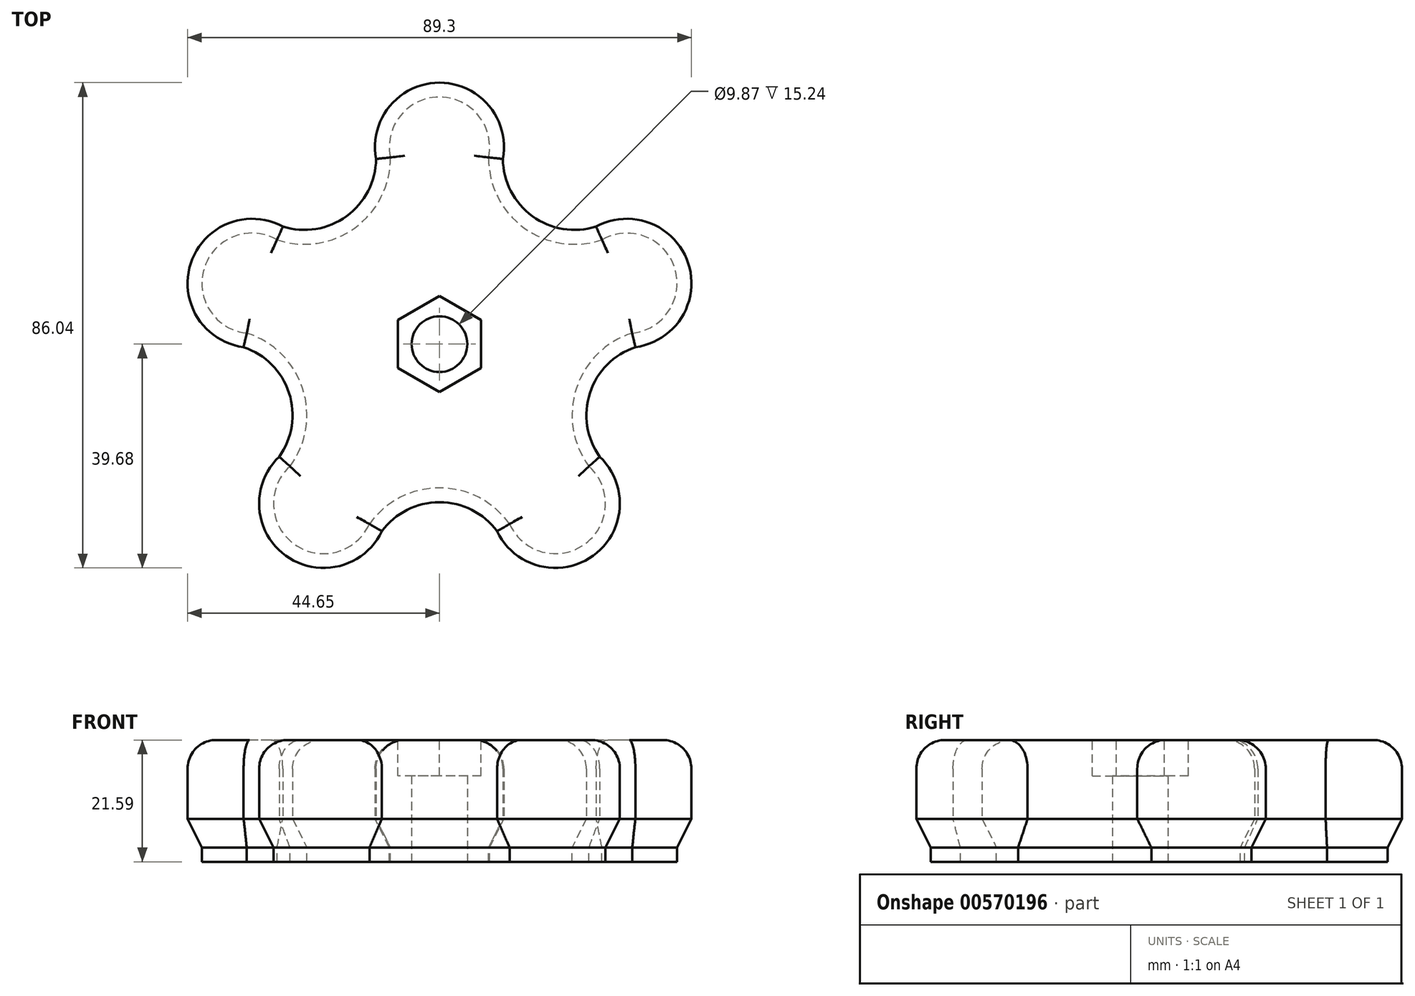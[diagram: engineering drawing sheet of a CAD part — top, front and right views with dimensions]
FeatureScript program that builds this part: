
annotation { "Feature Type Name" : "Feature", "Feature Type Description" : "" }
export const myFeature = defineFeature(function(context is Context, id is Id, definition is map)
    precondition{}
    {
        {
            var Q0;
            Q0=qCreatedBy(makeId("Top.planeOp"),FACE);
            var sketch = newSketch(context, id + "F0", { "sketchPlane" : qUnion([Q0])});
            skArc(sketch, "E0", {"start": v(11.24, 32.85) * mm, "mid": v(0, 46.36) * mm, "end": v(-11.24, 32.85) * mm});
            skArc(sketch, "E1.1.0", {"start": v(34.71, -0.54) * mm, "mid": v(44.09, 14.32) * mm, "end": v(27.77, 20.84) * mm});
            skArc(sketch, "E1.2.0", {"start": v(10.21, -33.18) * mm, "mid": v(27.25, -37.5) * mm, "end": v(28.4, -19.97) * mm});
            skArc(sketch, "E1.3.0", {"start": v(-28.4, -19.97) * mm, "mid": v(-27.25, -37.5) * mm, "end": v(-10.21, -33.18) * mm});
            skArc(sketch, "E1.4.0", {"start": v(-27.77, 20.84) * mm, "mid": v(-44.09, 14.32) * mm, "end": v(-34.71, -0.54) * mm});
            skPoint(sketch, "E1.center", {"position": v(0, 0) * mm});
            skLineSegment(sketch, "E1.anchor1", {"start": v(0, 0) * mm, "end": v(0, 34.93) * mm, "construction": true});
            skLineSegment(sketch, "E1.anchor2", {"start": v(0, 0) * mm, "end": v(-33.22, 10.8) * mm, "construction": true});
            skArc(sketch, "E2", {"start": v(-27.77, 20.84) * mm, "mid": v(-16.47, 22.67) * mm, "end": v(-11.24, 32.85) * mm});
            skArc(sketch, "E3.1.0", {"start": v(-28.4, -19.97) * mm, "mid": v(-26.66, -8.66) * mm, "end": v(-34.71, -0.54) * mm});
            skArc(sketch, "E3.2.0", {"start": v(10.21, -33.18) * mm, "mid": v(0, -28.03) * mm, "end": v(-10.21, -33.18) * mm});
            skArc(sketch, "E3.3.0", {"start": v(34.71, -0.54) * mm, "mid": v(26.66, -8.66) * mm, "end": v(28.4, -19.97) * mm});
            skArc(sketch, "E3.4.0", {"start": v(11.24, 32.85) * mm, "mid": v(16.47, 22.67) * mm, "end": v(27.77, 20.84) * mm});
            skCircle(sketch, "E4", {"center": v(0, 0) * mm, "radius": 4.93 * mm});
            skSolve(sketch);
        }
        {
            var Q0;
            Q0=makeQuery(id+"F0.imprint","IMPRINT",FACE,{"disambiguationData":[TD([[makeQuery(id+"F0.imprint","IMPRINT",EDGE,{"derivedFrom":sQuery(id+"F0.wireOp",EDGE,"E0")}),1.0]])]});
            extrude(context, id + "F1", {"entities" : qUnion([Q0]), "depth" : 19.05 * mm, "offsetDistance" : 25.4 * mm});
        }
        {
            var Q0;
            Q0=makeQuery(id+"F1.opExtrude","CAP_FACE",FACE,{"disambiguationData":[OSD([sQuery(id+"F0.wireOp",EDGE,"E0"),sQuery(id+"F0.wireOp",EDGE,"E1.1.0"),sQuery(id+"F0.wireOp",EDGE,"E1.2.0"),sQuery(id+"F0.wireOp",EDGE,"E1.3.0"),sQuery(id+"F0.wireOp",EDGE,"E1.4.0"),sQuery(id+"F0.wireOp",EDGE,"E2"),sQuery(id+"F0.wireOp",EDGE,"E3.1.0"),sQuery(id+"F0.wireOp",EDGE,"E3.2.0"),sQuery(id+"F0.wireOp",EDGE,"E3.3.0"),sQuery(id+"F0.wireOp",EDGE,"E3.4.0"),sQuery(id+"F0.wireOp",EDGE,"E4")])],"isStart":false});
            var sketch = newSketch(context, id + "F2", { "sketchPlane" : qUnion([Q0])});
            skCircle(sketch, "E5.cCircle", {"center": v(0, 0) * mm, "radius": 7.37 * mm, "construction": true});
            skLineSegment(sketch, "E5.0", {"start": v(-7.37, -4.25) * mm, "end": v(-7.37, 4.25) * mm});
            skLineSegment(sketch, "E5.1", {"start": v(-7.37, 4.25) * mm, "end": v(0, 8.5) * mm});
            skLineSegment(sketch, "E5.2", {"start": v(0, 8.5) * mm, "end": v(7.37, 4.25) * mm});
            skLineSegment(sketch, "E5.3", {"start": v(7.37, 4.25) * mm, "end": v(7.37, -4.25) * mm});
            skLineSegment(sketch, "E5.4", {"start": v(7.37, -4.25) * mm, "end": v(0, -8.5) * mm});
            skLineSegment(sketch, "E5.5", {"start": v(0, -8.5) * mm, "end": v(-7.37, -4.25) * mm});
            skPoint(sketch, "E5.0.midPoint", {"position": v(-7.37, 0) * mm});
            skSolve(sketch);
        }
        {
            var Q0;
            Q0=makeQuery(id+"F2.imprint","IMPRINT",FACE,{"disambiguationData":[TD([[makeQuery(id+"F2.imprint","IMPRINT",EDGE,{"derivedFrom":sQuery(id+"F2.wireOp",EDGE,"E5.0")}),-1.0]])]});
            extrude(context, id + "F3", {"entities" : qUnion([Q0]), "operationType" : NewBodyOperationType.REMOVE, "oppositeDirection" : true, "depth" : 6.35 * mm, "offsetDistance" : 25.4 * mm});
        }
        {
            var Q0;
            Q0=makeQuery(id+"F1.opExtrude","CAP_EDGE",EDGE,{"disambiguationData":[OSD([sQuery(id+"F0.wireOp",EDGE,"E3.1.0")])],"isStart":false});
            var Q1;
            Q1=makeQuery(id+"F1.opExtrude","CAP_EDGE",EDGE,{"disambiguationData":[OSD([sQuery(id+"F0.wireOp",EDGE,"E1.4.0")])],"isStart":false});
            var Q2;
            Q2=makeQuery(id+"F1.opExtrude","CAP_EDGE",EDGE,{"disambiguationData":[OSD([sQuery(id+"F0.wireOp",EDGE,"E2")])],"isStart":false});
            var Q3;
            Q3=makeQuery(id+"F1.opExtrude","CAP_EDGE",EDGE,{"disambiguationData":[OSD([sQuery(id+"F0.wireOp",EDGE,"E0")])],"isStart":false});
            var Q4;
            Q4=makeQuery(id+"F1.opExtrude","CAP_EDGE",EDGE,{"disambiguationData":[OSD([sQuery(id+"F0.wireOp",EDGE,"E3.4.0")])],"isStart":false});
            var Q5;
            Q5=makeQuery(id+"F1.opExtrude","CAP_EDGE",EDGE,{"disambiguationData":[OSD([sQuery(id+"F0.wireOp",EDGE,"E1.1.0")])],"isStart":false});
            var Q6;
            Q6=makeQuery(id+"F1.opExtrude","CAP_EDGE",EDGE,{"disambiguationData":[OSD([sQuery(id+"F0.wireOp",EDGE,"E3.3.0")])],"isStart":false});
            var Q7;
            Q7=makeQuery(id+"F1.opExtrude","CAP_EDGE",EDGE,{"disambiguationData":[OSD([sQuery(id+"F0.wireOp",EDGE,"E1.2.0")])],"isStart":false});
            var Q8;
            Q8=makeQuery(id+"F1.opExtrude","CAP_EDGE",EDGE,{"disambiguationData":[OSD([sQuery(id+"F0.wireOp",EDGE,"E3.2.0")])],"isStart":false});
            var Q9;
            Q9=makeQuery(id+"F1.opExtrude","CAP_EDGE",EDGE,{"disambiguationData":[OSD([sQuery(id+"F0.wireOp",EDGE,"E1.3.0")])],"isStart":false});
            fillet(context, id + "F4", {"entities" : qUnion([Q0, Q1, Q2, Q3, Q4, Q5, Q6, Q7, Q8, Q9]), "radius" : 5.08 * mm, "tangentPropagation" : true, "allowEdgeOverflow" : false});
        }
        {
            var Q0;
            Q0=makeQuery(id+"F1.opExtrude","CAP_EDGE",EDGE,{"disambiguationData":[OSD([sQuery(id+"F0.wireOp",EDGE,"E1.1.0")])],"isStart":true});
            var Q1;
            Q1=makeQuery(id+"F1.opExtrude","CAP_EDGE",EDGE,{"disambiguationData":[OSD([sQuery(id+"F0.wireOp",EDGE,"E3.4.0")])],"isStart":true});
            var Q2;
            Q2=makeQuery(id+"F1.opExtrude","CAP_EDGE",EDGE,{"disambiguationData":[OSD([sQuery(id+"F0.wireOp",EDGE,"E0")])],"isStart":true});
            var Q3;
            Q3=makeQuery(id+"F1.opExtrude","CAP_EDGE",EDGE,{"disambiguationData":[OSD([sQuery(id+"F0.wireOp",EDGE,"E2")])],"isStart":true});
            var Q4;
            Q4=makeQuery(id+"F1.opExtrude","CAP_EDGE",EDGE,{"disambiguationData":[OSD([sQuery(id+"F0.wireOp",EDGE,"E1.4.0")])],"isStart":true});
            var Q5;
            Q5=makeQuery(id+"F1.opExtrude","CAP_EDGE",EDGE,{"disambiguationData":[OSD([sQuery(id+"F0.wireOp",EDGE,"E3.1.0")])],"isStart":true});
            var Q6;
            Q6=makeQuery(id+"F1.opExtrude","CAP_EDGE",EDGE,{"disambiguationData":[OSD([sQuery(id+"F0.wireOp",EDGE,"E1.3.0")])],"isStart":true});
            var Q7;
            Q7=makeQuery(id+"F1.opExtrude","CAP_EDGE",EDGE,{"disambiguationData":[OSD([sQuery(id+"F0.wireOp",EDGE,"E3.2.0")])],"isStart":true});
            var Q8;
            Q8=makeQuery(id+"F1.opExtrude","CAP_EDGE",EDGE,{"disambiguationData":[OSD([sQuery(id+"F0.wireOp",EDGE,"E1.2.0")])],"isStart":true});
            var Q9;
            Q9=makeQuery(id+"F1.opExtrude","CAP_EDGE",EDGE,{"disambiguationData":[OSD([sQuery(id+"F0.wireOp",EDGE,"E3.3.0")])],"isStart":true});
            chamfer(context, id + "F5", {"entities" : qUnion([Q0, Q1, Q2, Q3, Q4, Q5, Q6, Q7, Q8, Q9]), "chamferType" : ChamferType.TWO_OFFSETS, "width1" : 5.08 * mm, "oppositeDirection" : false, "width2" : 2.54 * mm, "tangentPropagation" : true});
        }
        {
            var Q0;
            Q0=makeQuery(id+"F1.opExtrude","CAP_FACE",FACE,{"disambiguationData":[OSD([sQuery(id+"F0.wireOp",EDGE,"E0"),sQuery(id+"F0.wireOp",EDGE,"E1.1.0"),sQuery(id+"F0.wireOp",EDGE,"E1.2.0"),sQuery(id+"F0.wireOp",EDGE,"E1.3.0"),sQuery(id+"F0.wireOp",EDGE,"E1.4.0"),sQuery(id+"F0.wireOp",EDGE,"E2"),sQuery(id+"F0.wireOp",EDGE,"E3.1.0"),sQuery(id+"F0.wireOp",EDGE,"E3.2.0"),sQuery(id+"F0.wireOp",EDGE,"E3.3.0"),sQuery(id+"F0.wireOp",EDGE,"E3.4.0"),sQuery(id+"F0.wireOp",EDGE,"E4")])],"isStart":true});
            extrude(context, id + "F6", {"entities" : qUnion([Q0]), "operationType" : NewBodyOperationType.ADD, "depth" : 2.54 * mm, "offsetDistance" : 25.4 * mm});
        }
    });
